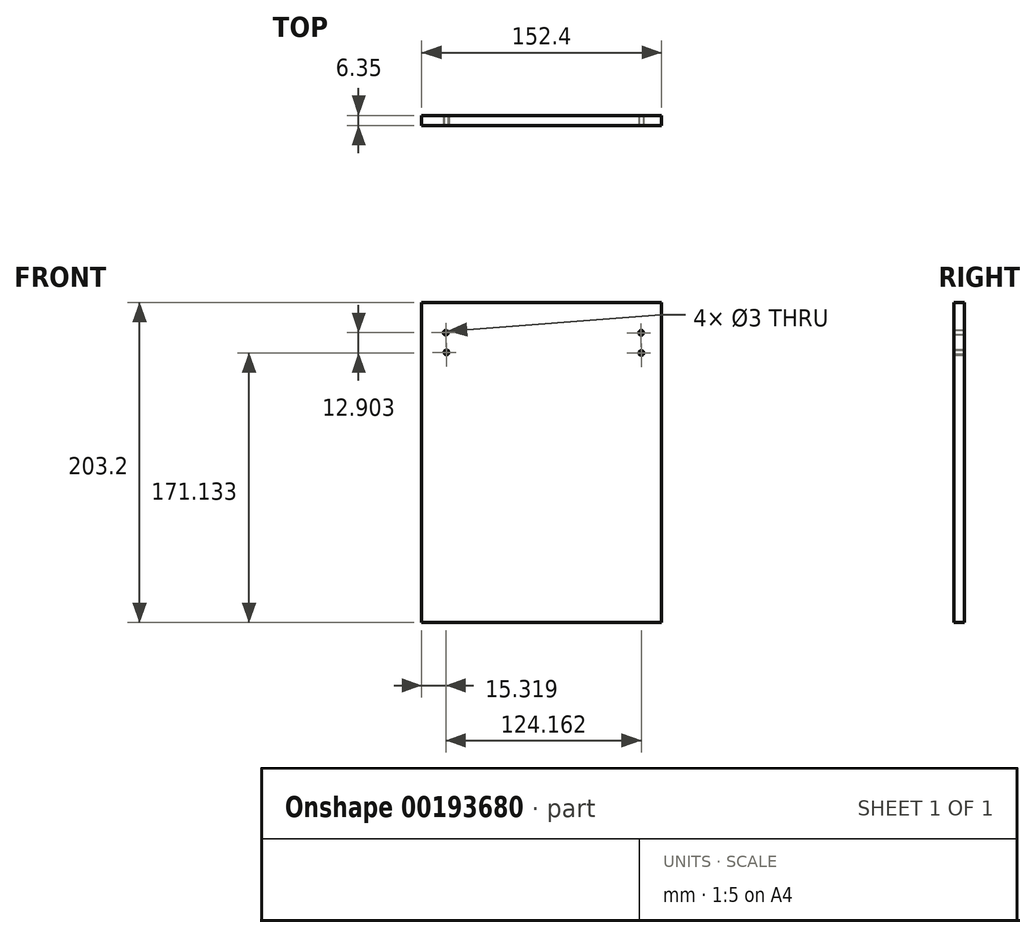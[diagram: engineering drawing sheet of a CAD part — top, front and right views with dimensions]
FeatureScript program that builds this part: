
annotation { "Feature Type Name" : "Feature", "Feature Type Description" : "" }
export const myFeature = defineFeature(function(context is Context, id is Id, definition is map)
    precondition{}
    {
        {
            var Q0;
            Q0=qCreatedBy(makeId("Front.planeOp"),FACE);
            var sketch = newSketch(context, id + "F0", { "sketchPlane" : qUnion([Q0])});
            skLineSegment(sketch, "E0.bottom", {"start": v(-76.2, 101.6) * mm, "end": v(76.2, 101.6) * mm});
            skLineSegment(sketch, "E0.top", {"start": v(-76.2, -101.6) * mm, "end": v(76.2, -101.6) * mm});
            skLineSegment(sketch, "E0.left", {"start": v(-76.2, 101.6) * mm, "end": v(-76.2, -101.6) * mm});
            skLineSegment(sketch, "E0.right", {"start": v(76.2, 101.6) * mm, "end": v(76.2, -101.6) * mm});
            skPoint(sketch, "E0.middle", {"position": v(0, 0) * mm});
            skSolve(sketch);
        }
        {
            var Q0;
            Q0=makeQuery(id+"F0.imprint","IMPRINT",FACE,{"disambiguationData":[TD([[makeQuery(id+"F0.imprint","IMPRINT",EDGE,{"derivedFrom":sQuery(id+"F0.wireOp",EDGE,"E0.bottom")}),-1.0]])]});
            extrude(context, id + "F1", {"entities" : qUnion([Q0]), "depth" : 6.35 * mm});
        }
        {
            var Q0;
            Q0=makeQuery(id+"F1.opExtrude","CAP_FACE",FACE,{"disambiguationData":[OSD([sQuery(id+"F0.wireOp",EDGE,"E0.bottom"),sQuery(id+"F0.wireOp",EDGE,"E0.top"),sQuery(id+"F0.wireOp",EDGE,"E0.left"),sQuery(id+"F0.wireOp",EDGE,"E0.right")])],"isStart":false});
            var sketch = newSketch(context, id + "F2", { "sketchPlane" : qUnion([Q0])});
            skLineSegment(sketch, "E1", {"start": v(-60.73, 101.6) * mm, "end": v(-60.73, 82.55) * mm});
            skLineSegment(sketch, "E2", {"start": v(-60.73, 82.55) * mm, "end": v(-60.73, 69.85) * mm});
            skSolve(sketch);
        }
        {
            var Q0;
            Q0=makeQuery(id+"F2.imprint","IMPRINT",FACE,{"disambiguationData":[TD([[makeQuery(id+"F2.imprint","IMPRINT",EDGE,{"derivedFrom":makeQuery(id+"F1.opExtrude","CAP_EDGE",EDGE,{"disambiguationData":[OSD([sQuery(id+"F0.wireOp",EDGE,"E0.top")])],"isStart":false})}),1.0]])]});
            var sketch = newSketch(context, id + "F3", { "sketchPlane" : qUnion([Q0])});
            skCircle(sketch, "E3", {"center": v(-60.88, 82.44) * mm, "radius": 1.5 * mm});
            skSolve(sketch);
        }
        {
            var Q0;
            Q0=makeQuery(id+"F2.imprint","IMPRINT",FACE,{"disambiguationData":[TD([[makeQuery(id+"F2.imprint","IMPRINT",EDGE,{"derivedFrom":makeQuery(id+"F1.opExtrude","CAP_EDGE",EDGE,{"disambiguationData":[OSD([sQuery(id+"F0.wireOp",EDGE,"E0.top")])],"isStart":false})}),1.0]])]});
            var sketch = newSketch(context, id + "F4", { "sketchPlane" : qUnion([Q0])});
            skCircle(sketch, "E4", {"center": v(-60.46, 69.95) * mm, "radius": 1.5 * mm});
            skSolve(sketch);
        }
        {
            var Q0;
            Q0 = qSketchRegion(id + "F3", true);
            var Q1;
            Q1=sQuery(id+"F3.wireOp",EDGE,"E3");
            extrude(context, id + "F5", {"entities" : qUnion([Q0]), "operationType" : NewBodyOperationType.REMOVE, "surfaceEntities" : qUnion([Q1]), "oppositeDirection" : true, "depth" : 6.35 * mm});
        }
        {
            var Q0;
            Q0 = qSketchRegion(id + "F4", true);
            var Q1;
            Q1=sQuery(id+"F4.wireOp",EDGE,"E4");
            extrude(context, id + "F6", {"entities" : qUnion([Q0]), "operationType" : NewBodyOperationType.REMOVE, "surfaceEntities" : qUnion([Q1]), "oppositeDirection" : true, "depth" : 6.35 * mm});
        }
        {
            var Q0;
            Q0=makeQuery(id+"F2.imprint","IMPRINT",FACE,{"disambiguationData":[TD([[makeQuery(id+"F2.imprint","IMPRINT",EDGE,{"derivedFrom":makeQuery(id+"F1.opExtrude","CAP_EDGE",EDGE,{"disambiguationData":[OSD([sQuery(id+"F0.wireOp",EDGE,"E0.top")])],"isStart":false})}),1.0]])]});
            var sketch = newSketch(context, id + "F7", { "sketchPlane" : qUnion([Q0])});
            skLineSegment(sketch, "E5", {"start": v(63.12, 101.37) * mm, "end": v(63.12, 82.32) * mm});
            skLineSegment(sketch, "E6", {"start": v(63.12, 82.32) * mm, "end": v(63.12, 69.62) * mm});
            skSolve(sketch);
        }
        {
            var Q0;
            Q0=makeQuery(id+"F2.imprint","IMPRINT",FACE,{"disambiguationData":[TD([[makeQuery(id+"F2.imprint","IMPRINT",EDGE,{"derivedFrom":makeQuery(id+"F1.opExtrude","CAP_EDGE",EDGE,{"disambiguationData":[OSD([sQuery(id+"F0.wireOp",EDGE,"E0.top")])],"isStart":false})}),1.0]])]});
            var sketch = newSketch(context, id + "F8", { "sketchPlane" : qUnion([Q0])});
            skCircle(sketch, "E7", {"center": v(63.2, 82.35) * mm, "radius": 1.5 * mm});
            skSolve(sketch);
        }
        {
            var Q0;
            Q0=makeQuery(id+"F2.imprint","IMPRINT",FACE,{"disambiguationData":[TD([[makeQuery(id+"F2.imprint","IMPRINT",EDGE,{"derivedFrom":makeQuery(id+"F1.opExtrude","CAP_EDGE",EDGE,{"disambiguationData":[OSD([sQuery(id+"F0.wireOp",EDGE,"E0.top")])],"isStart":false})}),1.0]])]});
            var sketch = newSketch(context, id + "F9", { "sketchPlane" : qUnion([Q0])});
            skCircle(sketch, "E8", {"center": v(63.28, 69.53) * mm, "radius": 1.5 * mm});
            skSolve(sketch);
        }
        {
            var Q0;
            Q0 = qSketchRegion(id + "F8", true);
            var Q1;
            Q1=sQuery(id+"F8.wireOp",EDGE,"E7");
            extrude(context, id + "F10", {"entities" : qUnion([Q0]), "operationType" : NewBodyOperationType.REMOVE, "surfaceEntities" : qUnion([Q1]), "oppositeDirection" : true, "depth" : 6.35 * mm});
        }
        {
            var Q0;
            Q0 = qSketchRegion(id + "F9", true);
            var Q1;
            Q1=sQuery(id+"F9.wireOp",EDGE,"E8");
            extrude(context, id + "F11", {"entities" : qUnion([Q0]), "operationType" : NewBodyOperationType.REMOVE, "surfaceEntities" : qUnion([Q1]), "oppositeDirection" : true, "depth" : 6.35 * mm});
        }
    });
